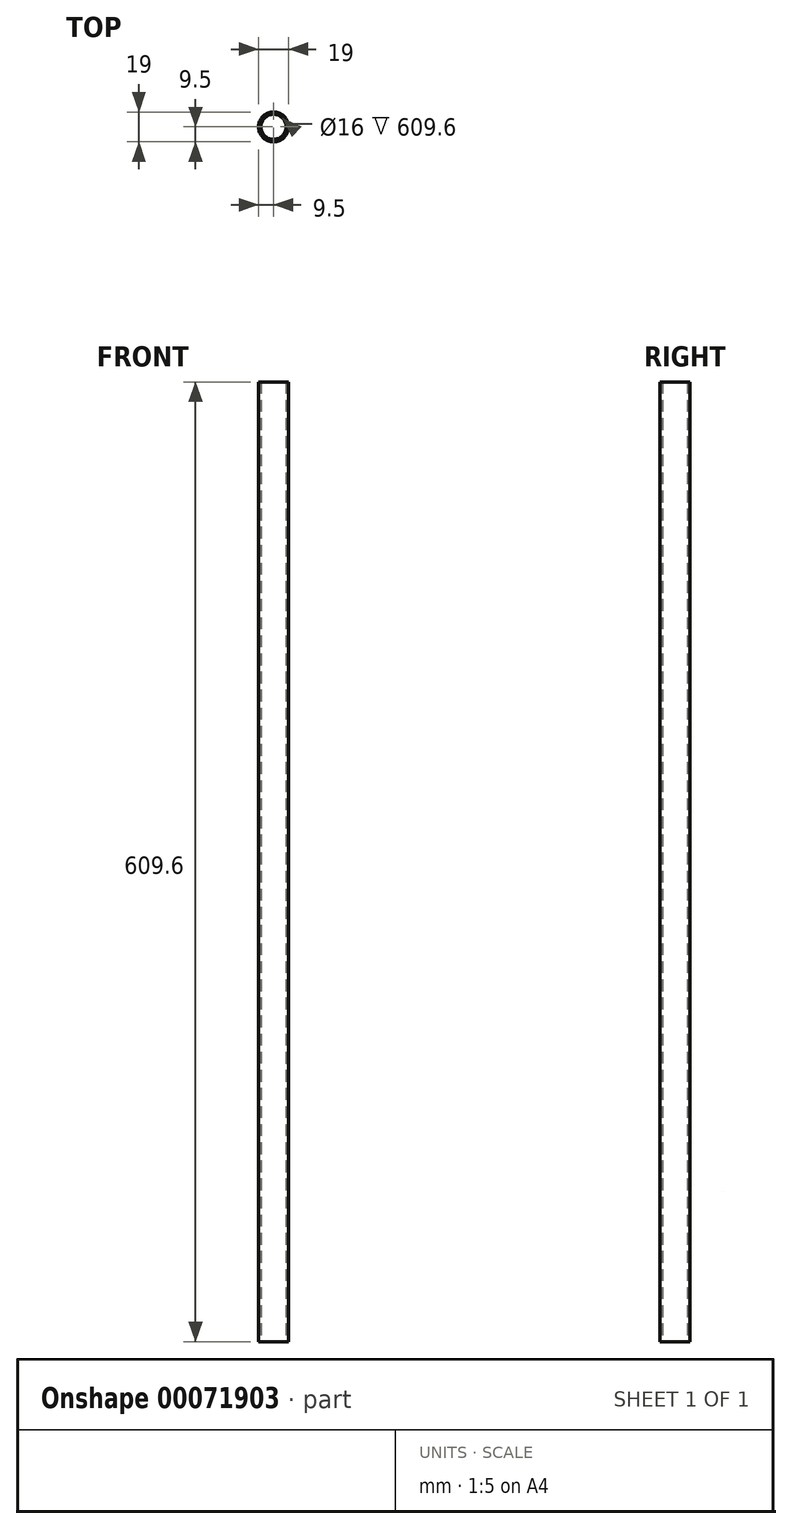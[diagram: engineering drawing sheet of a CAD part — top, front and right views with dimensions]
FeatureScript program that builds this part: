
annotation { "Feature Type Name" : "Feature", "Feature Type Description" : "" }
export const myFeature = defineFeature(function(context is Context, id is Id, definition is map)
    precondition{}
    {
        {
            var Q0;
            Q0=qCreatedBy(makeId("Top.planeOp"),FACE);
            var sketch = newSketch(context, id + "F0", { "sketchPlane" : qUnion([Q0])});
            skCircle(sketch, "E0", {"center": v(0, 0) * mm, "radius": 9.5 * mm});
            skCircle(sketch, "E1.0", {"center": v(0, 0) * mm, "radius": 8 * mm});
            skSolve(sketch);
        }
        {
            var Q0;
            Q0 = qSketchRegion(id + "F0", true);
            extrude(context, id + "F1", {"entities" : qUnion([Q0]), "depth" : 609.6 * mm, "offsetDistance" : 25 * mm});
        }
    });
